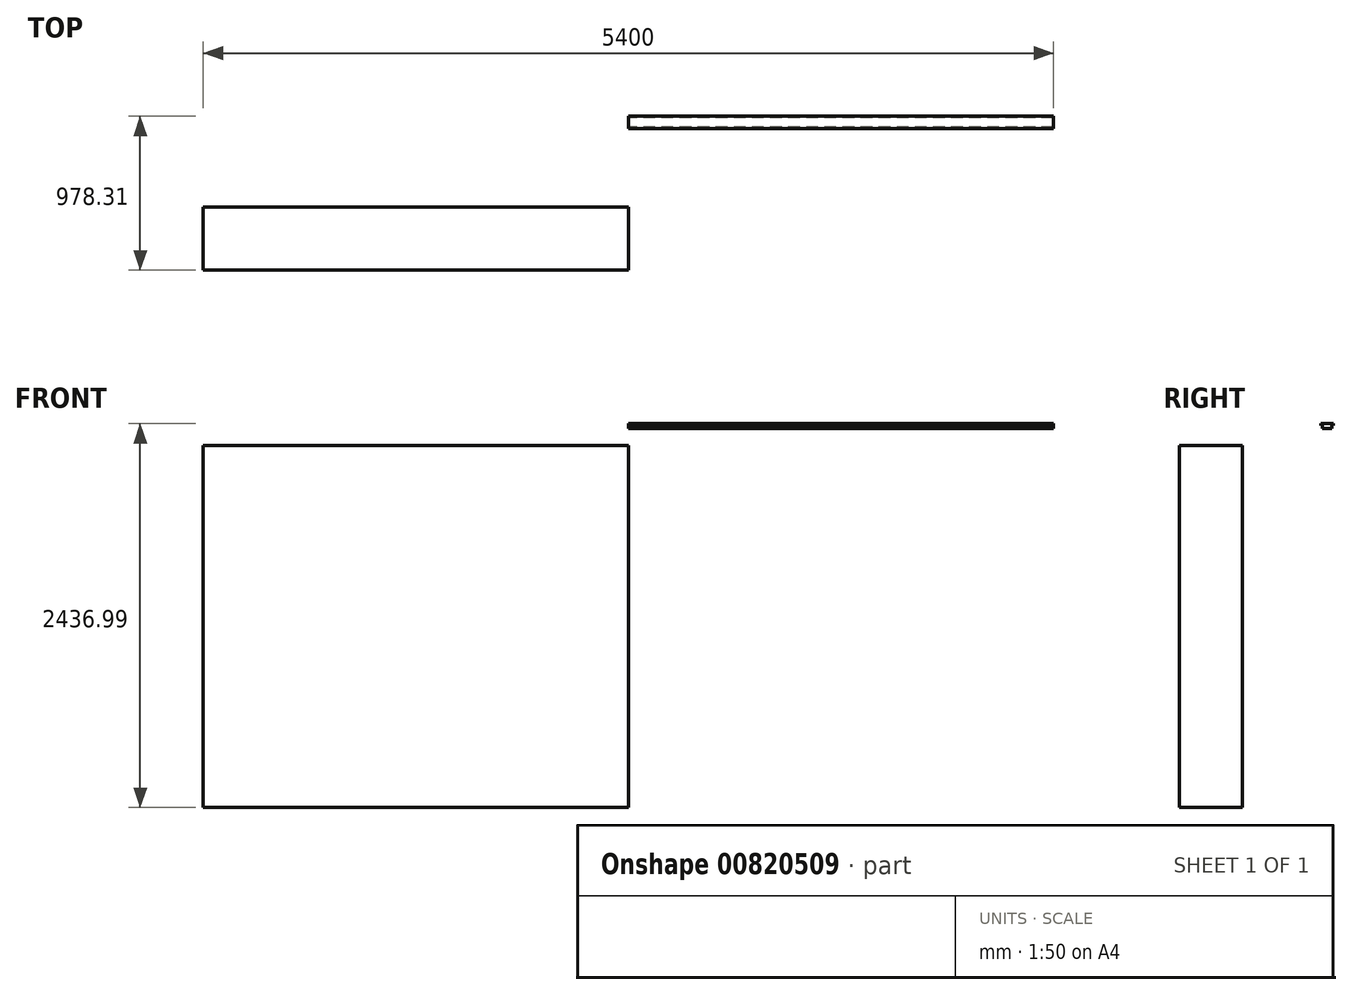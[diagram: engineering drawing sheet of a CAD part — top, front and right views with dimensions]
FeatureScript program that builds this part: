
annotation { "Feature Type Name" : "Feature", "Feature Type Description" : "" }
export const myFeature = defineFeature(function(context is Context, id is Id, definition is map)
    precondition{}
    {
        {
            var Q0;
            Q0=qCreatedBy(makeId("Right.planeOp"),FACE);
            var sketch = newSketch(context, id + "F0", { "sketchPlane" : qUnion([Q0])});
            skLineSegment(sketch, "E0", {"start": v(-30.76, -50.35) * mm, "end": v(369.24, -50.35) * mm});
            skLineSegment(sketch, "E1", {"start": v(369.24, -50.35) * mm, "end": v(369.24, 2249.65) * mm});
            skLineSegment(sketch, "E2", {"start": v(369.24, 2249.65) * mm, "end": v(-30.76, 2249.65) * mm});
            skLineSegment(sketch, "E3", {"start": v(-30.76, 2249.65) * mm, "end": v(-30.76, -50.35) * mm});
            skSolve(sketch);
        }
        {
            var Q0;
            Q0=makeQuery(id+"F0.imprint","IMPRINT",FACE,{"disambiguationData":[TD([[makeQuery(id+"F0.imprint","IMPRINT",EDGE,{"derivedFrom":sQuery(id+"F0.wireOp",EDGE,"E0")}),1.0]])]});
            extrude(context, id + "F1", {"entities" : qUnion([Q0]), "depth" : 2700 * mm, "offsetDistance" : 25 * mm});
        }
        {
            var Q0;
            Q0=makeQuery(id+"F1.opExtrude","CAP_FACE",FACE,{"disambiguationData":[OSD([sQuery(id+"F0.wireOp",EDGE,"E0"),sQuery(id+"F0.wireOp",EDGE,"E1"),sQuery(id+"F0.wireOp",EDGE,"E2"),sQuery(id+"F0.wireOp",EDGE,"E3")])],"isStart":false});
            var sketch = newSketch(context, id + "F2", { "sketchPlane" : qUnion([Q0])});
            skLineSegment(sketch, "E4", {"start": v(867.55, 2386.64) * mm, "end": v(947.55, 2386.64) * mm});
            skLineSegment(sketch, "E5", {"start": v(947.55, 2386.64) * mm, "end": v(947.55, 2376.64) * mm});
            skLineSegment(sketch, "E6", {"start": v(947.55, 2376.64) * mm, "end": v(937.55, 2376.64) * mm});
            skLineSegment(sketch, "E7", {"start": v(937.55, 2376.64) * mm, "end": v(937.55, 2356.64) * mm});
            skLineSegment(sketch, "E8", {"start": v(867.55, 2386.64) * mm, "end": v(867.55, 2376.64) * mm});
            skLineSegment(sketch, "E9", {"start": v(867.55, 2376.64) * mm, "end": v(877.55, 2376.64) * mm});
            skLineSegment(sketch, "E10", {"start": v(877.55, 2376.64) * mm, "end": v(877.55, 2356.64) * mm});
            skLineSegment(sketch, "E11", {"start": v(877.55, 2356.64) * mm, "end": v(937.55, 2356.64) * mm});
            skSolve(sketch);
        }
        {
            var Q0;
            Q0=makeQuery(id+"F2.imprint","IMPRINT",FACE,{"disambiguationData":[TD([[makeQuery(id+"F2.imprint","IMPRINT",EDGE,{"derivedFrom":sQuery(id+"F2.wireOp",EDGE,"E4")}),-1.0]])]});
            extrude(context, id + "F3", {"entities" : qUnion([Q0]), "depth" : 2700 * mm, "offsetDistance" : 25 * mm});
        }
    });
